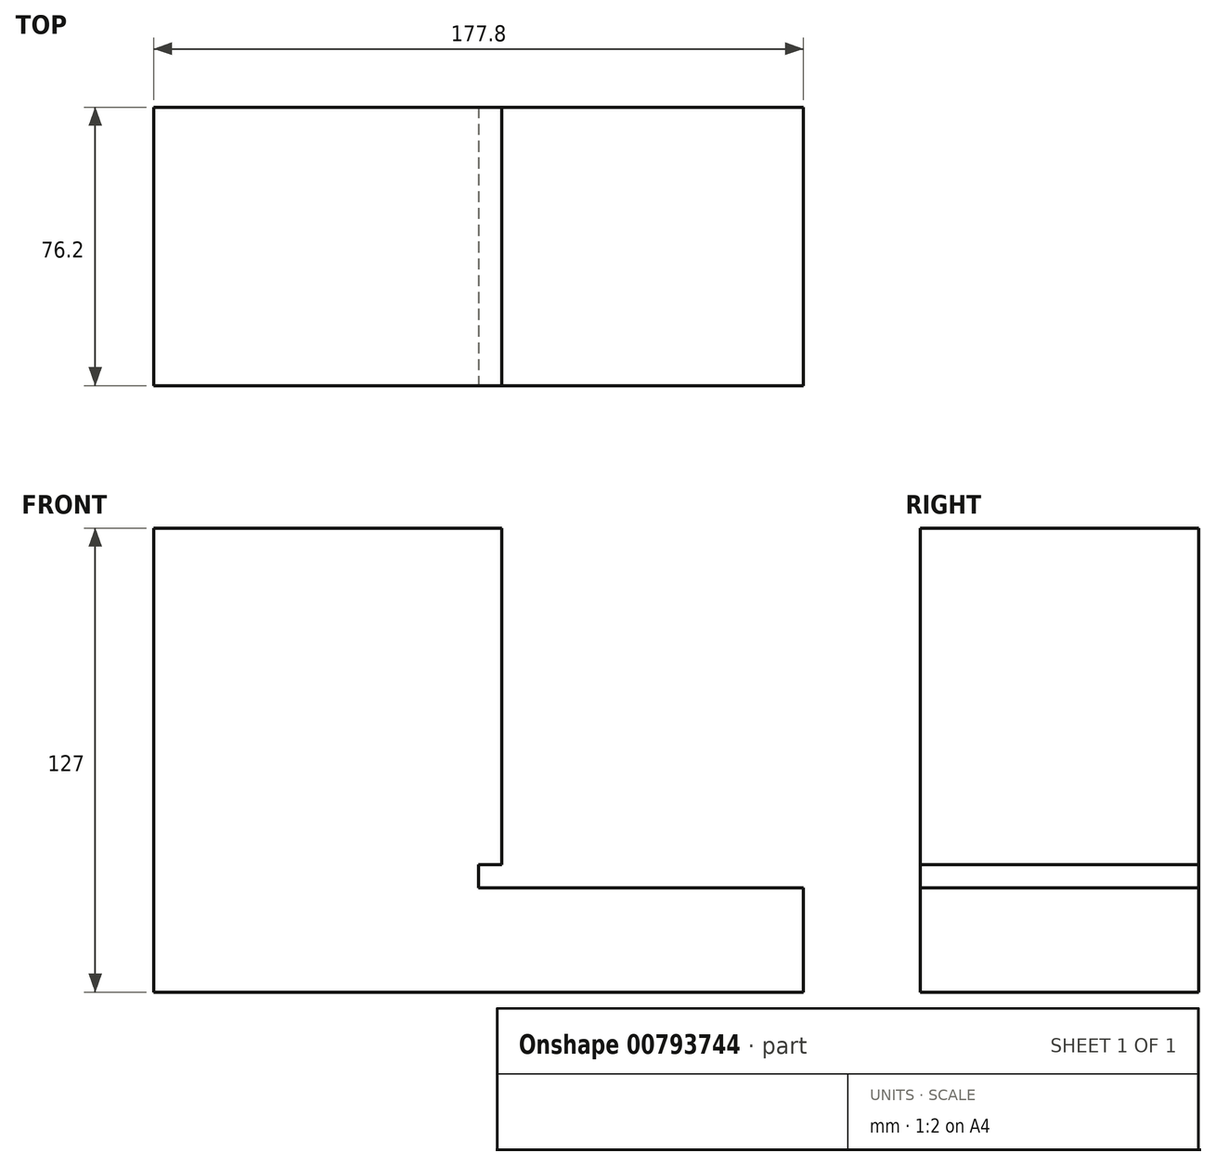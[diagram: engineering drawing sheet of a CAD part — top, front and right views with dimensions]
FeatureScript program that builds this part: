
annotation { "Feature Type Name" : "Feature", "Feature Type Description" : "" }
export const myFeature = defineFeature(function(context is Context, id is Id, definition is map)
    precondition{}
    {
        {
            var Q0;
            Q0=qCreatedBy(makeId("Front.planeOp"),FACE);
            var sketch = newSketch(context, id + "F0", { "sketchPlane" : qUnion([Q0])});
            skLineSegment(sketch, "E0", {"start": v(0, 0) * mm, "end": v(177.8, 0) * mm});
            skLineSegment(sketch, "E1", {"start": v(0, 0) * mm, "end": v(0, 127) * mm});
            skLineSegment(sketch, "E2", {"start": v(177.8, 0) * mm, "end": v(177.8, 127) * mm});
            skLineSegment(sketch, "E3", {"start": v(0, 127) * mm, "end": v(177.8, 127) * mm});
            skSolve(sketch);
        }
        {
            var Q0;
            Q0 = qSketchRegion(id + "F0", true);
            extrude(context, id + "F1", {"entities" : qUnion([Q0]), "depth" : 76.2 * mm, "offsetDistance" : 25.4 * mm});
        }
        {
            var Q0;
            Q0=makeQuery(id+"F1.opExtrude","SWEPT_FACE",FACE,{"disambiguationData":[OSD([sQuery(id+"F0.wireOp",EDGE,"E2")])]});
            var sketch = newSketch(context, id + "F2", { "sketchPlane" : qUnion([Q0])});
            skLineSegment(sketch, "E4", {"start": v(0, 0) * mm, "end": v(0, 34.93) * mm});
            skLineSegment(sketch, "E5", {"start": v(0, 34.93) * mm, "end": v(-76.2, 34.93) * mm});
            skSolve(sketch);
        }
        {
            var Q0;
            {var subQ0=sQuery(id+"F2.wireOp",EDGE,"E5");Q0=makeQuery(id+"F2.imprint","IMPRINT",FACE,{"disambiguationData":[TD([[makeQuery(id+"F2.imprint","IMPRINT",EDGE,{"derivedFrom":subQ0}),-1.0]])]});}
            extrude(context, id + "F3", {"entities" : qUnion([Q0]), "operationType" : NewBodyOperationType.REMOVE, "oppositeDirection" : true, "depth" : 82.55 * mm, "offsetDistance" : 25.4 * mm});
        }
        {
            var Q0;
            Q0=makeQuery(id+"F1.opExtrude","SWEPT_FACE",FACE,{"disambiguationData":[OSD([sQuery(id+"F0.wireOp",EDGE,"E2")])]});
            var sketch = newSketch(context, id + "F4", { "sketchPlane" : qUnion([Q0])});
            skLineSegment(sketch, "E6", {"start": v(0, 0) * mm, "end": v(0, 28.58) * mm});
            skLineSegment(sketch, "E7", {"start": v(0, 28.58) * mm, "end": v(-76.2, 28.58) * mm});
            skSolve(sketch);
        }
        {
            var Q0;
            {var subQ0=sQuery(id+"F4.wireOp",EDGE,"E7");Q0=makeQuery(id+"F4.imprint","IMPRINT",FACE,{"disambiguationData":[TD([[makeQuery(id+"F4.imprint","IMPRINT",EDGE,{"derivedFrom":subQ0}),-1.0]])]});}
            extrude(context, id + "F5", {"entities" : qUnion([Q0]), "operationType" : NewBodyOperationType.REMOVE, "oppositeDirection" : true, "depth" : 88.9 * mm, "offsetDistance" : 25.4 * mm});
        }
    });
